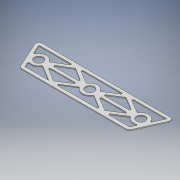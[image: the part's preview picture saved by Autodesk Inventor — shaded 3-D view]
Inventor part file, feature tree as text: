
AUTODESK INVENTOR PART (.ipt)
format: ipt  version: 2018.3 (Build 223284000, 284)  size: 252,416 bytes
history: native  units: mm
features: extrude x1, fillet x1, sketch x1
ambient origin geometry x8: Origin, YZ Plane, XZ Plane, XY Plane, X Axis, Y Axis, Z Axis, Center Point
bodies: Solid1 (feature_tree)
feature tree (3):
  extrude  "Extrusion1"  Depth=10.0mm
  fillet  "Fillet1"  Radius=10.0mm
  sketch  "Sketch1"  dims[d0=28.575mm d9=10.0mm d10=10.0mm d11=10.0mm d12=10.0mm d13=10.0mm d22=3.0mm d23=3.175mm d24=0.0mm d25=3.0mm]
